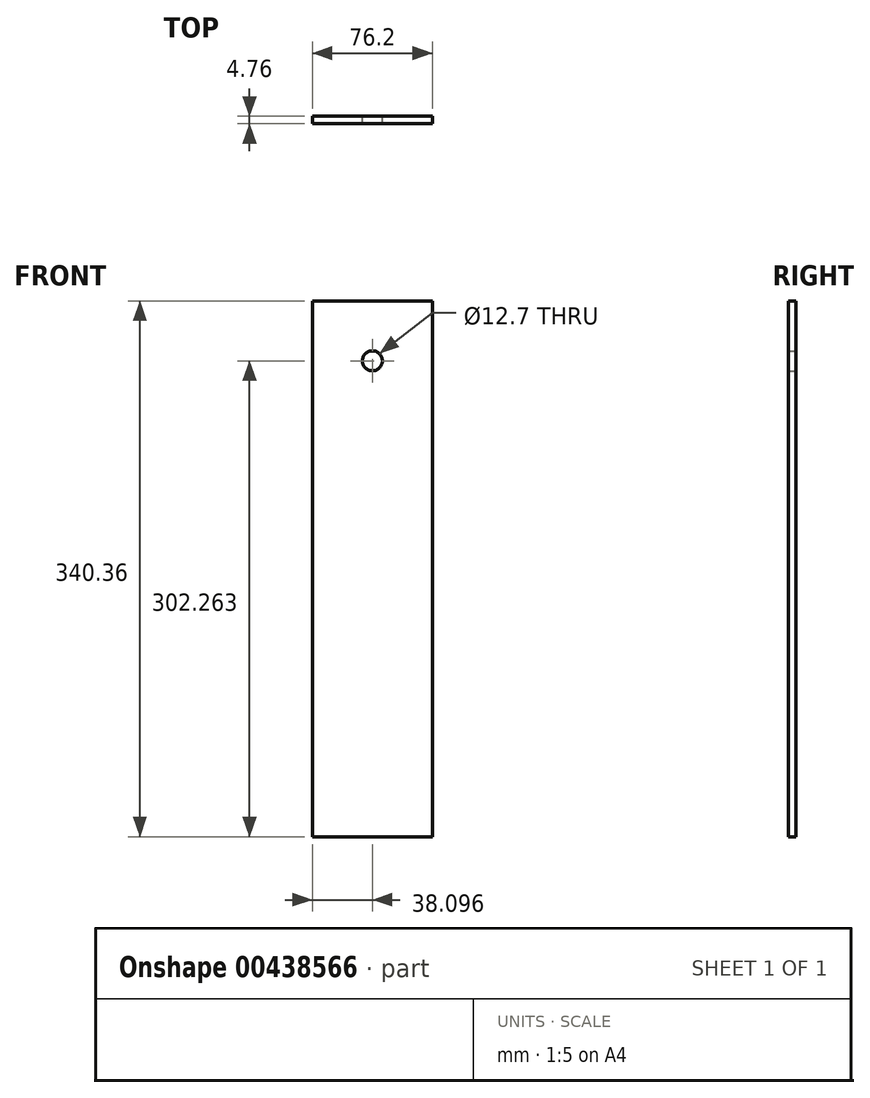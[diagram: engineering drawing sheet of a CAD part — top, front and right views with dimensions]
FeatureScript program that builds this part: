
annotation { "Feature Type Name" : "Feature", "Feature Type Description" : "" }
export const myFeature = defineFeature(function(context is Context, id is Id, definition is map)
    precondition{}
    {
        {
            var Q0;
            Q0=qCreatedBy(makeId("Front.planeOp"),FACE);
            var sketch = newSketch(context, id + "F0", { "sketchPlane" : qUnion([Q0])});
            skLineSegment(sketch, "E0.bottom", {"start": v(-47.77, 283.51) * mm, "end": v(28.43, 283.51) * mm});
            skLineSegment(sketch, "E0.top", {"start": v(-47.77, -56.85) * mm, "end": v(28.43, -56.85) * mm});
            skLineSegment(sketch, "E0.left", {"start": v(-47.77, 283.51) * mm, "end": v(-47.77, -56.85) * mm});
            skLineSegment(sketch, "E0.right", {"start": v(28.43, 283.51) * mm, "end": v(28.43, -56.85) * mm});
            skPoint(sketch, "E1", {"position": v(-9.67, 283.51) * mm});
            skPoint(sketch, "E2", {"position": v(-9.67, 245.41) * mm});
            skCircle(sketch, "E3", {"center": v(-9.67, 245.41) * mm, "radius": 6.35 * mm});
            skSolve(sketch);
        }
        {
            var Q0;
            Q0=makeQuery(id+"F0.imprint","IMPRINT",FACE,{"disambiguationData":[TD([[makeQuery(id+"F0.imprint","IMPRINT",EDGE,{"derivedFrom":sQuery(id+"F0.wireOp",EDGE,"E0.bottom")}),-1.0]])]});
            extrude(context, id + "F1", {"entities" : qUnion([Q0]), "depth" : 4.76 * mm});
        }
    });
